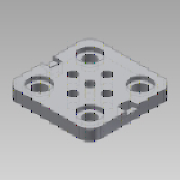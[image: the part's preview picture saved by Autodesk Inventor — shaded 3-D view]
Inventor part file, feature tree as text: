
AUTODESK INVENTOR PART (.ipt)
format: ipt  version: 2013 SP2 (Build 170200200, 200)  size: 208,896 bytes
history: native  units: mm
features: sketch x6, extrude x3, hole x3, fillet x1, plane x1, mirror x1
ambient origin geometry x8: Origin, YZ Plane, XZ Plane, XY Plane, X Axis, Y Axis, Z Axis, Center Point
bodies: Solid1 (feature_tree)
feature tree (15):
  extrude  "Extrusion1"  Depth=10.0mm
  hole  "Hole1"  [1 undecoded]
  hole  "Hole2"  [1 undecoded]
  sketch  "Sketch6"  dims[d16=15.0mm]
  hole  "Hole3"  [1 undecoded]
  fillet  "Fillet1"  Radius=2.5mm
  extrude  "Extrusion2"  Depth=5.25mm
  extrude  "Extrusion3"  Depth=6.7mm
  plane  "Work Plane1"
  mirror  "Mirror1"
  sketch  "Sketch1"  dims[d3=0.0mm d4=10.0mm]
  sketch  "Sketch2"  dims[d5=10.0mm d6=10.0mm]
  sketch  "Sketch4"  dims[d7=10.0mm]
  sketch  "Sketch5"  dims[d8=5.02mm d9=6.0mm d10=4.0mm d11=2.0mm d12=90.0deg d13=8.0mm d14=20.594885mm d15=15.0mm]
  sketch  "Sketch7"  dims[d17=7.14mm d18=6.0mm d19=12.0mm d20=2.18mm d21=90.0deg d22=6.35mm d23=0.0mm d24=6.17mm d25=2.5mm d27=5.25mm d28=6.7mm d29=6.35mm d30=0.0mm d31=2.18mm d33=6.35mm d34=0.0mm d35=31.9mm d36=5.0mm d37=6.0mm d38=10.1mm d39=2.0mm d40=90.0deg d41=8.0mm d42=20.594885mm]
note: 3 required parameter values undecoded (feature->parameter linkage not recoverable at this tier; creation-order binding heuristic only, values carry confidence <= 0.55)
